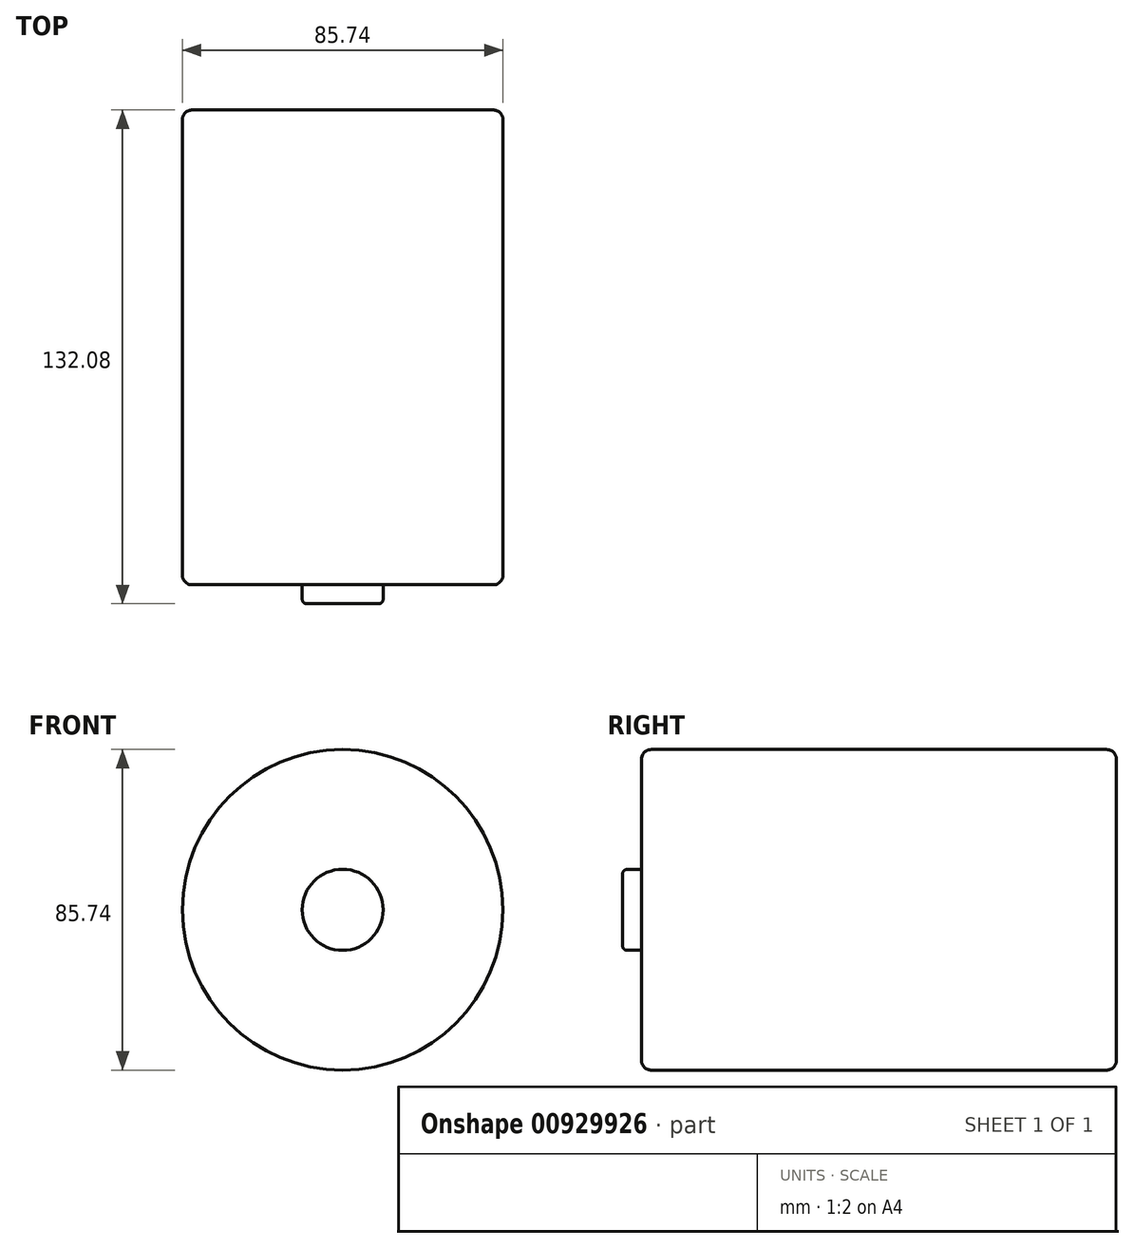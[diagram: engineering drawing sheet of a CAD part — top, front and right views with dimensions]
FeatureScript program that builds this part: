
annotation { "Feature Type Name" : "Feature", "Feature Type Description" : "" }
export const myFeature = defineFeature(function(context is Context, id is Id, definition is map)
    precondition{}
    {
        {
            var Q0;
            Q0=qCreatedBy(makeId("Front.planeOp"),FACE);
            var sketch = newSketch(context, id + "F0", { "sketchPlane" : qUnion([Q0])});
            skCircle(sketch, "E0", {"center": v(0, 0) * mm, "radius": 42.87 * mm});
            skSolve(sketch);
        }
        {
            var Q0;
            Q0=makeQuery(id+"F0.imprint","IMPRINT",FACE,{"disambiguationData":[TD([[makeQuery(id+"F0.imprint","IMPRINT",EDGE,{"derivedFrom":sQuery(id+"F0.wireOp",EDGE,"E0")}),1.0]])]});
            extrude(context, id + "F1", {"entities" : qUnion([Q0]), "depth" : 127 * mm, "offsetDistance" : 25.4 * mm});
        }
        {
            var Q0;
            Q0=makeQuery(id+"F1.opExtrude","SWEPT_FACE",FACE,{"disambiguationData":[OSD([sQuery(id+"F0.wireOp",EDGE,"E0")])]});
            var Q1;
            Q1=makeQuery(id+"F1.opExtrude","CAP_FACE",FACE,{"disambiguationData":[OSD([sQuery(id+"F0.wireOp",EDGE,"E0")])],"isStart":false});
            fillet(context, id + "F2", {"entities" : qUnion([Q0, Q1]), "radius" : 2.54 * mm, "tangentPropagation" : true, "allowEdgeOverflow" : false});
        }
        {
            var Q0;
            Q0=makeQuery(id+"F1.opExtrude","CAP_FACE",FACE,{"disambiguationData":[OSD([sQuery(id+"F0.wireOp",EDGE,"E0")])],"isStart":false});
            var sketch = newSketch(context, id + "F3", { "sketchPlane" : qUnion([Q0])});
            skCircle(sketch, "E1", {"center": v(0, 0) * mm, "radius": 10.83 * mm});
            skSolve(sketch);
        }
        {
            var Q0;
            Q0=makeQuery(id+"F3.imprint","IMPRINT",FACE,{"disambiguationData":[TD([[makeQuery(id+"F3.imprint","IMPRINT",EDGE,{"derivedFrom":sQuery(id+"F3.wireOp",EDGE,"E1")}),1.0]])]});
            extrude(context, id + "F4", {"entities" : qUnion([Q0]), "operationType" : NewBodyOperationType.ADD, "depth" : 5.08 * mm, "offsetDistance" : 25.4 * mm});
        }
        {
            var Q0;
            Q0=makeQuery(id+"F4.opExtrude","CAP_EDGE",EDGE,{"disambiguationData":[OSD([sQuery(id+"F3.wireOp",EDGE,"E1")])],"isStart":false});
            fillet(context, id + "F5", {"entities" : qUnion([Q0]), "radius" : 1.27 * mm, "tangentPropagation" : true, "allowEdgeOverflow" : false});
        }
    });
